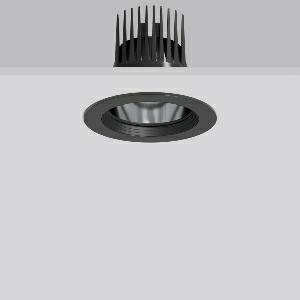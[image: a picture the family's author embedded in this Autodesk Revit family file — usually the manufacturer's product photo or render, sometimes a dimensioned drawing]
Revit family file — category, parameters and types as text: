
# Revit family: heledon_maxi_e_901756_003_76_1add
name_source: partatom
category: Lighting Fixtures
units: mm (PartAtom-declared; Revit-internal decimal feet)

## family parameters
Cut with Voids When Loaded = No
Host = Face
Light Source = No
Part Type = Normal
Room Calculation Point = No
Round Connector Dimension = Use Diameter
Shared = No

## types (1)
- HELEDON maxi E (1 x LED Modul 930, 3250 lm, 3000)
    Apparent Load = 25 VA
    Approval mark = CE
    CIE Flux Codes = 100 100 100 100 100
    Color Rendering = 90
    Color Temperature = 3000
    Default Elevation = 1800 mm
    Description = Series: HELEDON maxi
Round recessed downlight. Housing: die-cast aluminium, powder-coated. Black plastic ring and recessed LED to prevent glare from the side. Optical assembly with reflector made of MIRO-Silver with 98% total light reflection for outstanding efficiency - can be changed without tools. Best colour rendering index Ra>90. Suitable for Recessed ceiling mounting. Installation without tools thanks to spring fastening system. Including separate LED converter with connecting cable 600 mm.High quality converter without flickering and stroboscopic effect. Through-wiring box (5 pole) available as accessory. The following accessories can be mounted without use of tools: interchangeable lenses, decorative glasses, honeycomb louvre, clear and frosted diffusers, white interchangeable plastic ring. 
Colour: deep black, matt (RAL 9005)
Diameter: 162 mm
Height: 3 mm
Cut-out diameter: 152 mm
Recess height: 200 mm
Luminaire: recess height: 135 mm
Lamp: LED
Socket: without socket
Colour temperature: 3000K
Colour rendering index (CRI): 92
System power: 25 W
Rated luminous flux: 3250 lm
Luminous efficiency: 130 lm/W
Control gear: Converter, dimmable, DALI
Protection class: II
Type of protection: IP 20
    Height = 0 mm  [stored 0 ft]
    Lamp = 1 x LED Modul 930
    Lamp Light Flux = 3250 lm
    Lamp count = 1
    Length = 162 mm
    Lifetime = 50000 h
    Luminous efficacy = 130 lm/W
    Manufacturer = RZB
    ModVariant = No
    Model = 901756.003.76
    Mounting Place = Ceiling
    Mounting Type = Recessed
    Number of Poles = 1
    OnlyDefault = Yes
    Power Factor = 1
    Product Name = HELEDON maxi E
    Product group = Recessed downlights
    ProductGroupID = 402
    Protection Class = Protection class II
    Protection Degree = IP 20
    RLX_Detail_Level = 1
    RLX_Emergency_Light_Flux = 0 lm
    RLX_Emergency_Type = 0
    RLX_Emergency_Type_DB = No
    RlxData = <blob elided: 122233 chars, md5=e26b5d79>
    Socket = socket
    Standby Power = 0 W
    System Light Flux = 3250 lm
    System Power = 25 W
    Type Comments = Product without accessories
    Type Image = 901662.003.jpg
    URL = http://relux.com
    VarID = ---
    Voltage = 230 V
    Voltage Range = 220-240 V
    Weight = 0.00 kg
    Width = 0 mm  [stored 0 ft]

note: [stored X ft] marks values corroborated as IEEE doubles in the binary element streams (Revit-internal decimal feet)

## geometry (parser evidence)
native form markers: Blend x4, Sweep x11
no freeform markers — native parametric forms only
